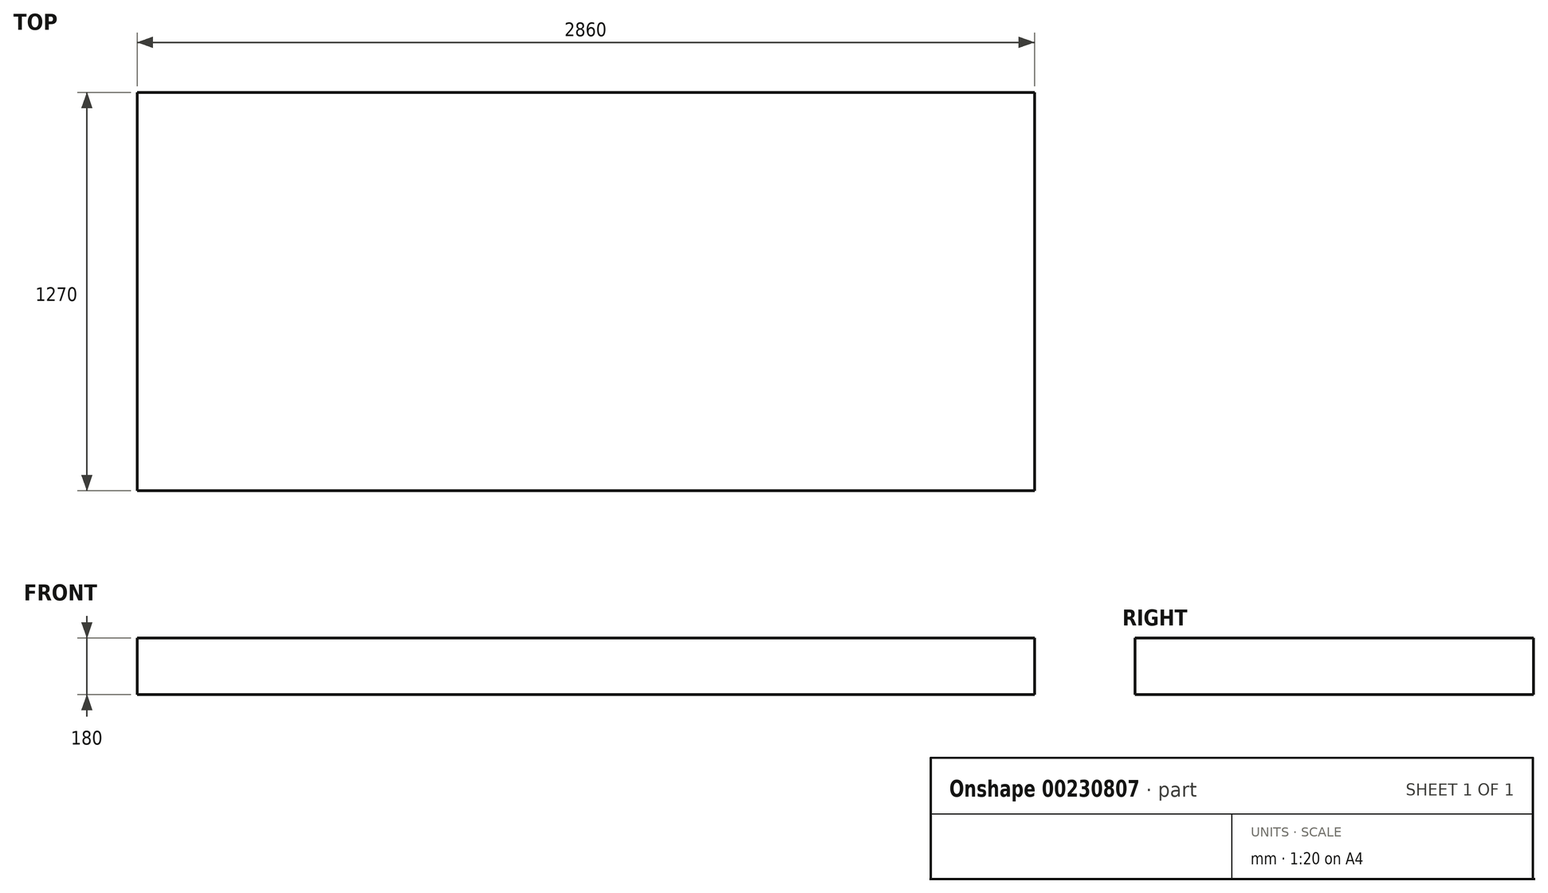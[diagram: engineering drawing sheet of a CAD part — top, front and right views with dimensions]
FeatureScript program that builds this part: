
annotation { "Feature Type Name" : "Feature", "Feature Type Description" : "" }
export const myFeature = defineFeature(function(context is Context, id is Id, definition is map)
    precondition{}
    {
        {
            var Q0;
            Q0=qCreatedBy(makeId("Front.planeOp"),FACE);
            var sketch = newSketch(context, id + "F0", { "sketchPlane" : qUnion([Q0])});
            skLineSegment(sketch, "E0.bottom", {"start": v(-1260.06, -156.4) * mm, "end": v(1599.94, -156.4) * mm});
            skLineSegment(sketch, "E0.top", {"start": v(-1260.06, -336.4) * mm, "end": v(1599.94, -336.4) * mm});
            skLineSegment(sketch, "E0.left", {"start": v(-1260.06, -156.4) * mm, "end": v(-1260.06, -336.4) * mm});
            skLineSegment(sketch, "E0.right", {"start": v(1599.94, -156.4) * mm, "end": v(1599.94, -336.4) * mm});
            skSolve(sketch);
        }
        {
            var Q0;
            Q0 = qSketchRegion(id + "F0", true);
            extrude(context, id + "F1", {"entities" : qUnion([Q0]), "depth" : 1270 * mm});
        }
    });
